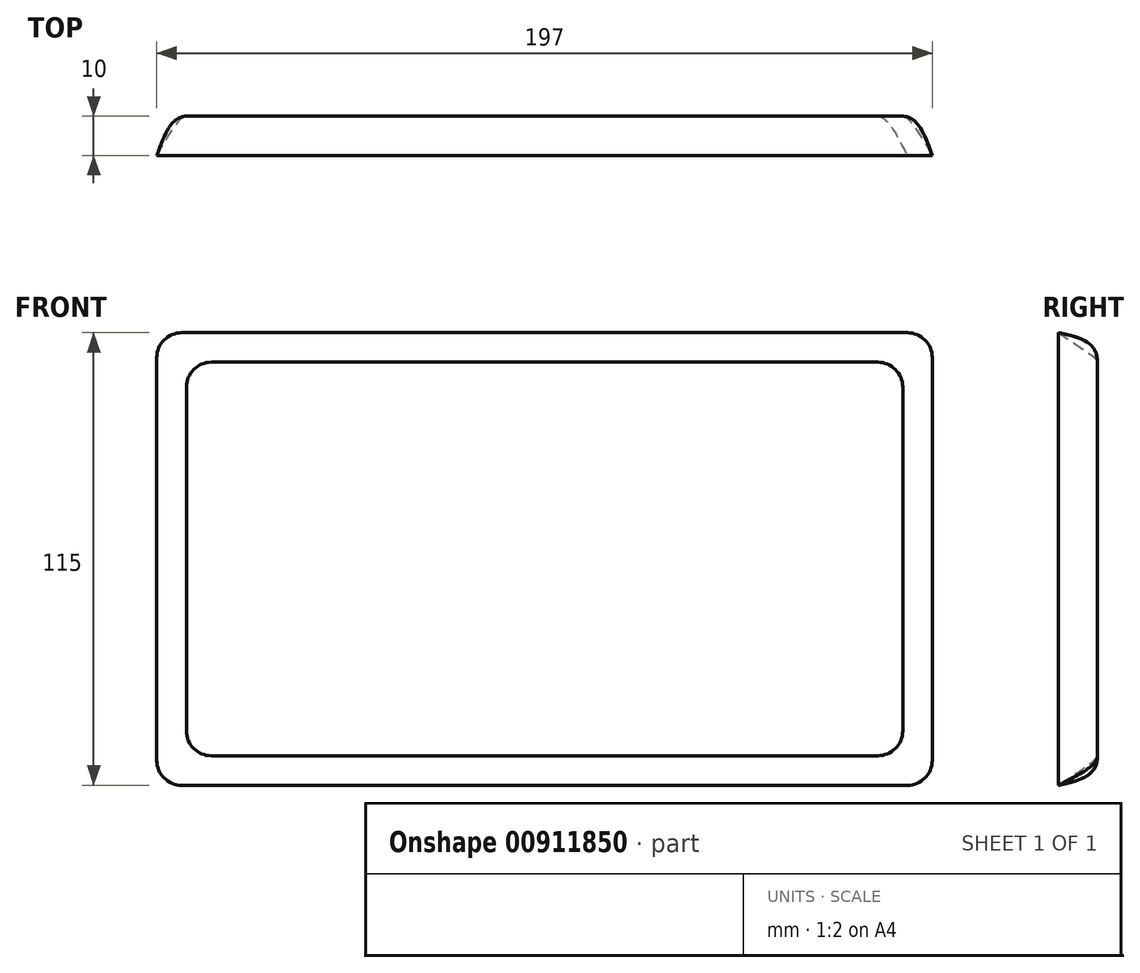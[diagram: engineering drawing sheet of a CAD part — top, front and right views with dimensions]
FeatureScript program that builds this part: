
annotation { "Feature Type Name" : "Feature", "Feature Type Description" : "" }
export const myFeature = defineFeature(function(context is Context, id is Id, definition is map)
    precondition{}
    {
        {
            var Q0;
            Q0=qCreatedBy(makeId("Front.planeOp"),FACE);
            var sketch = newSketch(context, id + "F0", { "sketchPlane" : qUnion([Q0])});
            skLineSegment(sketch, "E0.bottom", {"start": v(-6.35, 0) * mm, "end": v(-190.65, 0) * mm});
            skLineSegment(sketch, "E0.top", {"start": v(-6.35, -115) * mm, "end": v(-190.65, -115) * mm});
            skLineSegment(sketch, "E0.left", {"start": v(0, -6.35) * mm, "end": v(0, -108.65) * mm});
            skLineSegment(sketch, "E0.right", {"start": v(-197, -6.35) * mm, "end": v(-197, -108.65) * mm});
            skPoint(sketch, "E1.visualSharp", {"position": v(-197, 0) * mm});
            skArc(sketch, "E1.filletArc", {"start": v(-190.65, 0) * mm, "mid": v(-195.14, -1.86) * mm, "end": v(-197, -6.35) * mm});
            skPoint(sketch, "E2.visualSharp", {"position": v(0, 0) * mm});
            skArc(sketch, "E2.filletArc", {"start": v(0, -6.35) * mm, "mid": v(-1.86, -1.86) * mm, "end": v(-6.35, 0) * mm});
            skPoint(sketch, "E3.visualSharp", {"position": v(0, -115) * mm});
            skArc(sketch, "E3.filletArc", {"start": v(-6.35, -115) * mm, "mid": v(-1.86, -113.14) * mm, "end": v(0, -108.65) * mm});
            skPoint(sketch, "E4.visualSharp", {"position": v(-197, -115) * mm});
            skArc(sketch, "E4.filletArc", {"start": v(-197, -108.65) * mm, "mid": v(-195.14, -113.14) * mm, "end": v(-190.65, -115) * mm});
            skPoint(sketch, "E5.visualSharp", {"position": v(-189.5, -7.5) * mm});
            skPoint(sketch, "E6.visualSharp", {"position": v(-7.5, -7.5) * mm});
            skPoint(sketch, "E7.visualSharp", {"position": v(-7.5, -107.5) * mm});
            skPoint(sketch, "E8.visualSharp", {"position": v(-189.5, -107.5) * mm});
            skPoint(sketch, "E9.visualSharp", {"position": v(-196.8, -0.2) * mm});
            skPoint(sketch, "E10.visualSharp", {"position": v(-196.8, -114.8) * mm});
            skPoint(sketch, "E11.visualSharp", {"position": v(-0.2, -114.8) * mm});
            skPoint(sketch, "E12.visualSharp", {"position": v(-0.2, -0.2) * mm});
            skSolve(sketch);
        }
        {
            var Q0;
            Q0=makeQuery(id+"F0.imprint","IMPRINT",FACE,{"disambiguationData":[TD([[makeQuery(id+"F0.imprint","IMPRINT",EDGE,{"derivedFrom":sQuery(id+"F0.wireOp",EDGE,"E0.bottom")}),1.0]])]});
            cPlane(context, id + "F1", {"entities" : qUnion([Q0]), "cplaneType" : CPlaneType.OFFSET, "offset" : 10 * mm, "oppositeDirection" : true, "width" : 150 * mm, "height" : 150 * mm});
        }
        {
            var Q0;
            Q0=qCreatedBy(id+"F1.planeOp",FACE);
            var sketch = newSketch(context, id + "F2", { "sketchPlane" : qUnion([Q0])});
            skLineSegment(sketch, "E13.0.0", {"start": v(-183.15, -107.5) * mm, "end": v(-13.85, -107.5) * mm});
            skArc(sketch, "E13.0.1", {"start": v(-13.85, -107.5) * mm, "mid": v(-9.36, -105.64) * mm, "end": v(-7.5, -101.15) * mm});
            skLineSegment(sketch, "E13.0.2", {"start": v(-7.5, -101.15) * mm, "end": v(-7.5, -13.85) * mm});
            skArc(sketch, "E13.0.3", {"start": v(-7.5, -13.85) * mm, "mid": v(-9.36, -9.36) * mm, "end": v(-13.85, -7.5) * mm});
            skLineSegment(sketch, "E13.0.4", {"start": v(-13.85, -7.5) * mm, "end": v(-183.15, -7.5) * mm});
            skArc(sketch, "E13.0.5", {"start": v(-183.15, -7.5) * mm, "mid": v(-187.64, -9.36) * mm, "end": v(-189.5, -13.85) * mm});
            skLineSegment(sketch, "E13.0.6", {"start": v(-189.5, -13.85) * mm, "end": v(-189.5, -101.15) * mm});
            skArc(sketch, "E13.0.7", {"start": v(-189.5, -101.15) * mm, "mid": v(-187.64, -105.64) * mm, "end": v(-183.15, -107.5) * mm});
            skSolve(sketch);
        }
        {
            var Q0;
            Q0=makeQuery(id+"F2.imprint","IMPRINT",FACE,{"disambiguationData":[TD([[makeQuery(id+"F2.imprint","IMPRINT",EDGE,{"derivedFrom":sQuery(id+"F2.wireOp",EDGE,"E13.0.0")}),1.0]])]});
            var Q1;
            Q1=makeQuery(id+"F0.imprint","IMPRINT",FACE,{"disambiguationData":[TD([[makeQuery(id+"F0.imprint","IMPRINT",EDGE,{"derivedFrom":sQuery(id+"F0.wireOp",EDGE,"E0.bottom")}),1.0]])]});
            var Q2;
            Q2=makeQuery(id+"F2.imprint","IMPRINT",FACE,{"disambiguationData":[TD([[makeQuery(id+"F2.imprint","IMPRINT",EDGE,{"derivedFrom":sQuery(id+"F2.wireOp",EDGE,"E13.0.0")}),1.0]])]});
            var Q3;
            Q3=makeQuery(id+"F0.imprint","IMPRINT",FACE,{"disambiguationData":[TD([[makeQuery(id+"F0.imprint","IMPRINT",EDGE,{"derivedFrom":sQuery(id+"F0.wireOp",EDGE,"E0.bottom")}),1.0]])]});
            loft(context, id + "F3", {"bodyType" : ToolBodyType.SURFACE, "operationType" : NewBodyOperationType.REMOVE, "startCondition" : LoftEndDerivativeType.TANGENT_TO_PROFILE, "startMagnitude" : 1, "sheetProfilesArray" : [{ "sheetProfileEntities" : qUnion([Q0]) }, { "sheetProfileEntities" : qUnion([Q1]) }], "wireProfilesArray" : [{ "wireProfileEntities" : qUnion([Q2]) }, { "wireProfileEntities" : qUnion([Q3]) }]});
        }
    });
